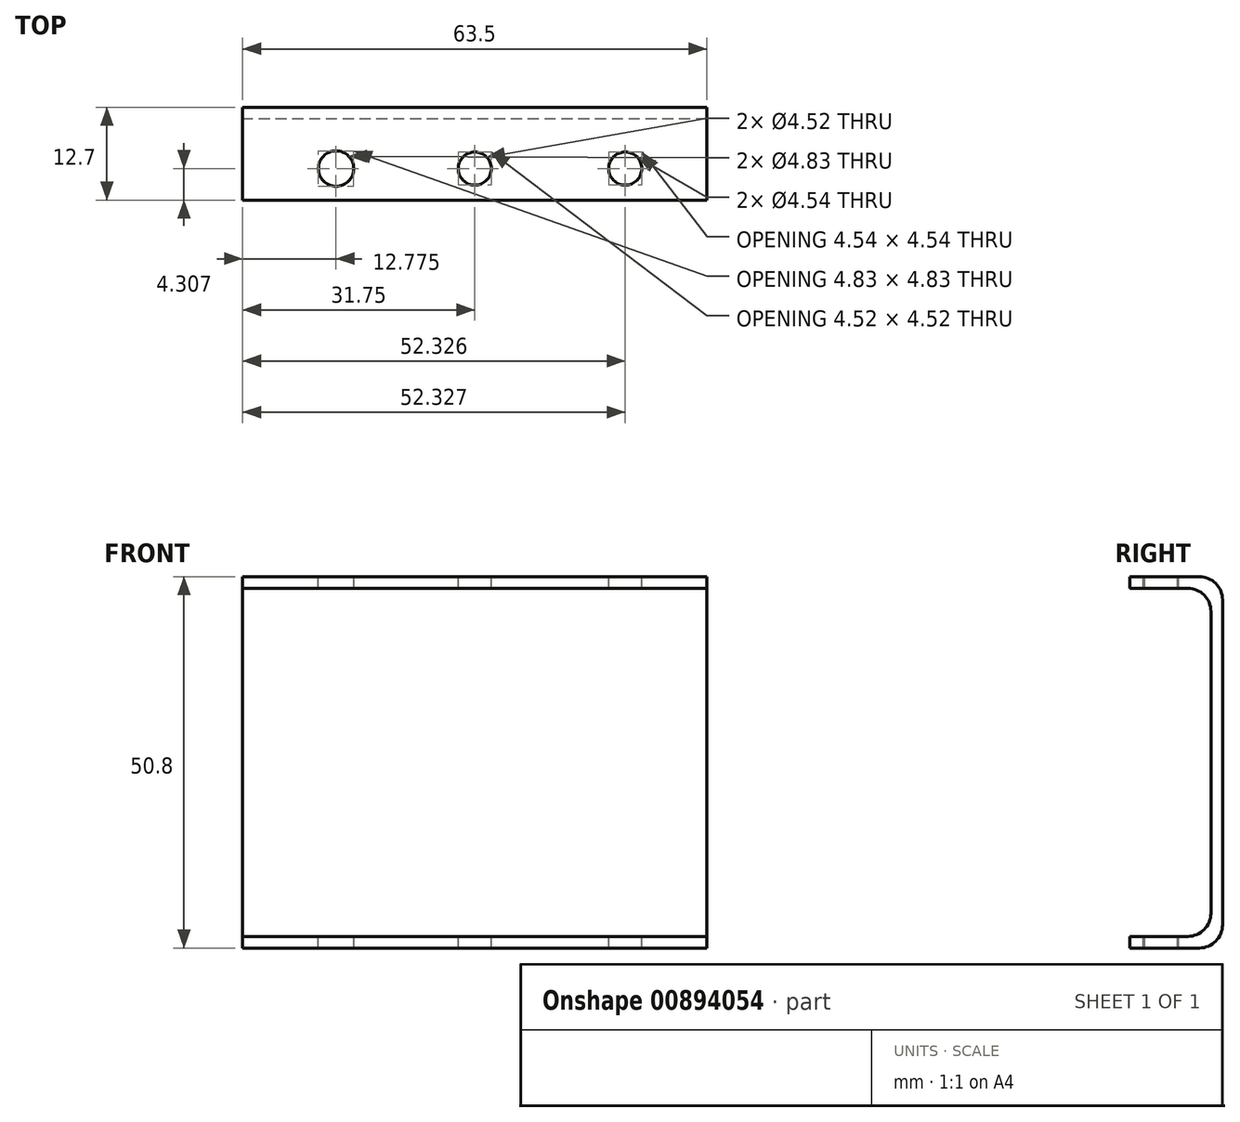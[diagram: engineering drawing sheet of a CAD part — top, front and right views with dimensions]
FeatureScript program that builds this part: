
annotation { "Feature Type Name" : "Feature", "Feature Type Description" : "" }
export const myFeature = defineFeature(function(context is Context, id is Id, definition is map)
    precondition{}
    {
        {
            var Q0;
            Q0=qCreatedBy(makeId("Right.planeOp"),FACE);
            var sketch = newSketch(context, id + "F0", { "sketchPlane" : qUnion([Q0])});
            skLineSegment(sketch, "E0", {"start": v(0.8, 0) * mm, "end": v(0.8, 22.23) * mm});
            skLineSegment(sketch, "E1", {"start": v(-2.38, 25.4) * mm, "end": v(-11.9, 25.4) * mm});
            skLineSegment(sketch, "E2", {"start": v(-11.9, 25.4) * mm, "end": v(-11.9, 23.81) * mm});
            skLineSegment(sketch, "E3", {"start": v(-11.9, 23.81) * mm, "end": v(-3.97, 23.81) * mm});
            skLineSegment(sketch, "E4", {"start": v(-0.8, 20.64) * mm, "end": v(-0.8, 0) * mm});
            skLineSegment(sketch, "E5", {"start": v(-0.8, 0) * mm, "end": v(0.8, 0) * mm});
            skPoint(sketch, "E6.visualSharp", {"position": v(-0.8, 23.81) * mm});
            skArc(sketch, "E6.filletArc", {"start": v(-0.8, 20.64) * mm, "mid": v(-1.72, 22.88) * mm, "end": v(-3.97, 23.81) * mm});
            skPoint(sketch, "E7.visualSharp", {"position": v(0.8, 25.4) * mm});
            skArc(sketch, "E7.filletArc", {"start": v(0.8, 22.23) * mm, "mid": v(-0.14, 24.47) * mm, "end": v(-2.38, 25.4) * mm});
            skLineSegment(sketch, "E8.MirrorCS", {"start": v(-11.9, -25.4) * mm, "end": v(-11.9, -23.81) * mm});
            skLineSegment(sketch, "E9.MirrorCS", {"start": v(-0.8, -20.64) * mm, "end": v(-0.8, 0) * mm});
            skPoint(sketch, "E10.MirrorP", {"position": v(-0.8, -23.81) * mm});
            skArc(sketch, "E11.MirrorCS", {"start": v(-0.8, -20.64) * mm, "mid": v(-1.72, -22.88) * mm, "end": v(-3.97, -23.81) * mm});
            skLineSegment(sketch, "E12.MirrorCS", {"start": v(-2.38, -25.4) * mm, "end": v(-11.9, -25.4) * mm});
            skLineSegment(sketch, "E13.MirrorCS", {"start": v(-11.9, -23.81) * mm, "end": v(-3.97, -23.81) * mm});
            skLineSegment(sketch, "E14.MirrorCS", {"start": v(0.8, 0) * mm, "end": v(0.8, -22.23) * mm});
            skArc(sketch, "E15.MirrorCS", {"start": v(0.8, -22.23) * mm, "mid": v(-0.14, -24.47) * mm, "end": v(-2.38, -25.4) * mm});
            skPoint(sketch, "E16.MirrorP", {"position": v(0.8, -25.4) * mm});
            skSolve(sketch);
        }
        {
            var Q0;
            Q0 = qSketchRegion(id + "F0", true);
            extrude(context, id + "F1", {"entities" : qUnion([Q0]), "endBound" : BoundingType.SYMMETRIC, "depth" : 63.5 * mm, "offsetDistance" : 25.4 * mm});
        }
        {
            var Q0;
            Q0=qCreatedBy(makeId("Top.planeOp"),FACE);
            var sketch = newSketch(context, id + "F2", { "sketchPlane" : qUnion([Q0])});
            skCircle(sketch, "E17", {"center": v(0, -7.6) * mm, "radius": 2.26 * mm});
            skCircle(sketch, "E18", {"center": v(-18.97, -7.6) * mm, "radius": 2.42 * mm});
            skCircle(sketch, "E19", {"center": v(20.58, -7.6) * mm, "radius": 2.27 * mm});
            skSolve(sketch);
        }
        {
            var Q0;
            Q0 = qSketchRegion(id + "F2", true);
            extrude(context, id + "F3", {"entities" : qUnion([Q0]), "operationType" : NewBodyOperationType.REMOVE, "endBound" : BoundingType.THROUGH_ALL, "oppositeDirection" : true, "depth" : 25.4 * mm, "offsetDistance" : 25.4 * mm, "hasSecondDirection" : true, "secondDirectionBound" : SecondDirectionBoundingType.THROUGH_ALL, "secondDirectionOppositeDirection" : false, "secondDirectionDepth" : 25.4 * mm});
        }
    });
